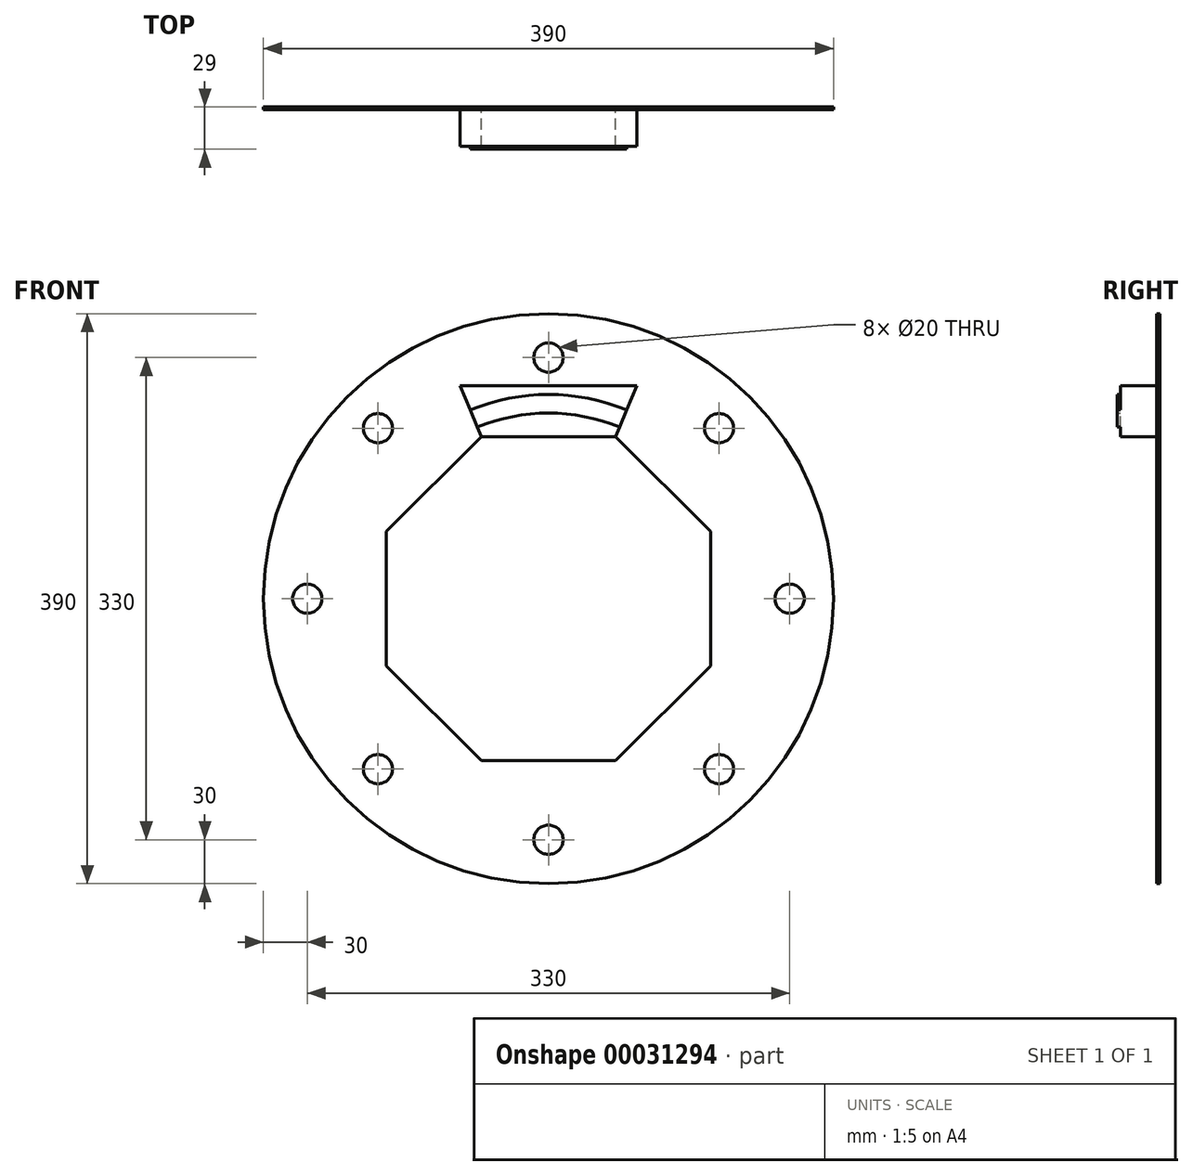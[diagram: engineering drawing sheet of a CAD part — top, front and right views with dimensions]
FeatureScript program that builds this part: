
annotation { "Feature Type Name" : "Feature", "Feature Type Description" : "" }
export const myFeature = defineFeature(function(context is Context, id is Id, definition is map)
    precondition{}
    {
        {
            var Q0;
            Q0=qCreatedBy(makeId("Front.planeOp"),FACE);
            var sketch = newSketch(context, id + "F0", { "sketchPlane" : qUnion([Q0])});
            skCircle(sketch, "E0", {"center": v(0, 0) * mm, "radius": 127 * mm, "construction": true});
            skCircle(sketch, "E1", {"center": v(0, 0) * mm, "radius": 139.7 * mm, "construction": true});
            skCircle(sketch, "E2.cCircle", {"center": v(0, 0) * mm, "radius": 110.9 * mm, "construction": true});
            skLineSegment(sketch, "E2.0", {"start": v(-110.9, -45.93) * mm, "end": v(-110.9, 45.93) * mm});
            skLineSegment(sketch, "E2.1", {"start": v(-110.9, 45.93) * mm, "end": v(-45.93, 110.9) * mm});
            skLineSegment(sketch, "E2.2", {"start": v(-45.93, 110.9) * mm, "end": v(45.93, 110.9) * mm});
            skLineSegment(sketch, "E2.3", {"start": v(45.93, 110.9) * mm, "end": v(110.9, 45.93) * mm});
            skLineSegment(sketch, "E2.4", {"start": v(110.9, 45.93) * mm, "end": v(110.9, -45.93) * mm});
            skLineSegment(sketch, "E2.5", {"start": v(110.9, -45.93) * mm, "end": v(45.93, -110.9) * mm});
            skLineSegment(sketch, "E2.6", {"start": v(45.93, -110.9) * mm, "end": v(-45.93, -110.9) * mm});
            skLineSegment(sketch, "E2.7", {"start": v(-45.93, -110.9) * mm, "end": v(-110.9, -45.93) * mm});
            skPoint(sketch, "E2.0.midPoint", {"position": v(-110.9, 0) * mm});
            skCircle(sketch, "E3.cCircle", {"center": v(0, 0) * mm, "radius": 145.8 * mm, "construction": true});
            skLineSegment(sketch, "E3.0", {"start": v(-145.8, -60.4) * mm, "end": v(-145.8, 60.4) * mm});
            skLineSegment(sketch, "E3.1", {"start": v(-145.8, 60.4) * mm, "end": v(-60.4, 145.8) * mm});
            skLineSegment(sketch, "E3.2", {"start": v(-60.4, 145.8) * mm, "end": v(60.4, 145.8) * mm});
            skLineSegment(sketch, "E3.3", {"start": v(60.4, 145.8) * mm, "end": v(145.8, 60.4) * mm});
            skLineSegment(sketch, "E3.4", {"start": v(145.8, 60.4) * mm, "end": v(145.8, -60.4) * mm});
            skLineSegment(sketch, "E3.5", {"start": v(145.8, -60.4) * mm, "end": v(60.4, -145.8) * mm});
            skLineSegment(sketch, "E3.6", {"start": v(60.4, -145.8) * mm, "end": v(-60.4, -145.8) * mm});
            skLineSegment(sketch, "E3.7", {"start": v(-60.4, -145.8) * mm, "end": v(-145.8, -60.4) * mm});
            skPoint(sketch, "E3.0.midPoint", {"position": v(-145.8, 0) * mm});
            skLineSegment(sketch, "E4", {"start": v(-145.8, 60.4) * mm, "end": v(-110.9, 45.93) * mm});
            skLineSegment(sketch, "E5", {"start": v(-60.4, 145.8) * mm, "end": v(-45.93, 110.9) * mm});
            skLineSegment(sketch, "E6", {"start": v(60.4, 145.8) * mm, "end": v(45.93, 110.9) * mm});
            skLineSegment(sketch, "E7", {"start": v(145.8, 60.4) * mm, "end": v(110.9, 45.93) * mm});
            skLineSegment(sketch, "E8", {"start": v(145.8, -60.4) * mm, "end": v(110.9, -45.93) * mm});
            skLineSegment(sketch, "E9", {"start": v(60.4, -145.8) * mm, "end": v(45.93, -110.9) * mm});
            skLineSegment(sketch, "E10", {"start": v(-60.4, -145.8) * mm, "end": v(-45.93, -110.9) * mm});
            skLineSegment(sketch, "E11", {"start": v(-145.8, -60.4) * mm, "end": v(-110.9, -45.93) * mm});
            skLineSegment(sketch, "E12", {"start": v(-117.33, 48.6) * mm, "end": v(-129.07, 53.46) * mm});
            skSolve(sketch);
        }
        {
            var Q0;
            Q0=makeQuery(id+"F0.imprint","IMPRINT",FACE,{"disambiguationData":[TD([[makeQuery(id+"F0.imprint","IMPRINT",EDGE,{"derivedFrom":sQuery(id+"F0.wireOp",EDGE,"E2.2")}),1.0]])]});
            extrude(context, id + "F1", {"entities" : qUnion([Q0]), "depth" : 25 * mm});
        }
        {
            var Q0;
            Q0=makeQuery(id+"F1.opExtrude","CAP_FACE",FACE,{"disambiguationData":[OSD([sQuery(id+"F0.wireOp",EDGE,"E2.2"),sQuery(id+"F0.wireOp",EDGE,"E3.2"),sQuery(id+"F0.wireOp",EDGE,"E5"),sQuery(id+"F0.wireOp",EDGE,"E6")])],"isStart":false});
            var sketch = newSketch(context, id + "F2", { "sketchPlane" : qUnion([Q0])});
            skArc(sketch, "E13", {"start": v(-48.6, 117.33) * mm, "mid": v(0, 127) * mm, "end": v(48.6, 117.33) * mm});
            skArc(sketch, "E14", {"start": v(-53.46, 129.07) * mm, "mid": v(0, 139.7) * mm, "end": v(53.46, 129.07) * mm});
            skLineSegment(sketch, "E15", {"start": v(53.46, 129.07) * mm, "end": v(48.6, 117.33) * mm});
            skLineSegment(sketch, "E16", {"start": v(-48.6, 117.33) * mm, "end": v(-53.46, 129.07) * mm});
            skPoint(sketch, "E17", {"position": v(0, 139.7) * mm});
            skSolve(sketch);
        }
        {
            var Q0;
            Q0 = qSketchRegion(id + "F2", true);
            extrude(context, id + "F3", {"entities" : qUnion([Q0]), "operationType" : NewBodyOperationType.ADD, "depth" : 2 * mm, "offsetDistance" : 25 * mm});
        }
        {
            var Q0;
            Q0=makeQuery(id+"F0.imprint","IMPRINT",FACE,{"disambiguationData":[TD([[makeQuery(id+"F0.imprint","IMPRINT",EDGE,{"derivedFrom":sQuery(id+"F0.wireOp",EDGE,"E2.0")}),-1.0]])]});
            var sketch = newSketch(context, id + "F4", { "sketchPlane" : qUnion([Q0])});
            skCircle(sketch, "E18", {"center": v(0, 0) * mm, "radius": 195 * mm});
            skLineSegment(sketch, "E19", {"start": v(0, 0) * mm, "end": v(0, -235.02) * mm, "construction": true});
            skLineSegment(sketch, "E20", {"start": v(0, -235.02) * mm, "end": v(0, 217.7) * mm, "construction": true});
            skLineSegment(sketch, "E21", {"start": v(0, 0) * mm, "end": v(326.87, 0) * mm, "construction": true});
            skLineSegment(sketch, "E22", {"start": v(0, 0) * mm, "end": v(-275.73, 0) * mm, "construction": true});
            skPoint(sketch, "E23", {"position": v(0, 165) * mm});
            skCircle(sketch, "E24", {"center": v(0, 165) * mm, "radius": 10 * mm});
            skCircle(sketch, "E25.1.0", {"center": v(116.67, 116.67) * mm, "radius": 10 * mm});
            skCircle(sketch, "E25.2.0", {"center": v(165, 0) * mm, "radius": 10 * mm});
            skCircle(sketch, "E25.3.0", {"center": v(116.67, -116.67) * mm, "radius": 10 * mm});
            skCircle(sketch, "E25.4.0", {"center": v(0, -165) * mm, "radius": 10 * mm});
            skCircle(sketch, "E25.5.0", {"center": v(-116.67, -116.67) * mm, "radius": 10 * mm});
            skCircle(sketch, "E25.6.0", {"center": v(-165, 0) * mm, "radius": 10 * mm});
            skCircle(sketch, "E25.7.0", {"center": v(-116.67, 116.67) * mm, "radius": 10 * mm});
            skLineSegment(sketch, "E25.anchor1", {"start": v(0, 0) * mm, "end": v(0, 165) * mm, "construction": true});
            skLineSegment(sketch, "E25.anchor2", {"start": v(0, 0) * mm, "end": v(-116.67, 116.67) * mm, "construction": true});
            skPoint(sketch, "E26", {"position": v(0, 195) * mm});
            skPoint(sketch, "E27", {"position": v(0, 175) * mm});
            skPoint(sketch, "E28", {"position": v(0, 155) * mm});
            skSolve(sketch);
        }
        {
            var Q0;
            Q0=makeQuery(id+"F4.imprint","IMPRINT",FACE,{"disambiguationData":[TD([[makeQuery(id+"F4.imprint","IMPRINT",EDGE,{"derivedFrom":sQuery(id+"F4.wireOp",EDGE,"E18")}),1.0]])]});
            extrude(context, id + "F5", {"entities" : qUnion([Q0]), "operationType" : NewBodyOperationType.ADD, "oppositeDirection" : true, "depth" : 2 * mm, "offsetDistance" : 25 * mm});
        }
    });
